# Revit family: Haworth_BeHold_OverheadStorage_Open_SingleSided
name_source: partatom
category: Furniture Systems
revit_build: Autodesk Revit 2018 (Build: 20170223_1515(x64)
units: mm (PartAtom-declared; Revit-internal decimal feet)

## family parameters
Always vertical = Yes
Cut with Voids When Loaded = No
OmniClass Number = 23.40.70.14.64.21
OmniClass Title = Systems Furniture
Part Type = Normal
Room Calculation Point = No
Round Connector Dimension = Use Diameter
Shared = No
Work Plane-Based = No

## types (4) — shared parameters
Actual Depth = 14.7 "
Assembly Code = E2020200
Back Finish = Haworth _ Laminate _ Beige H-34
Cabinet Finish = Haworth _ Laminate _ Beige H-34
Custom Size = No
Manufacturer = Haworth
Max. Height = 16 "
Max. Width = 72 "
Min. Height = 8 "
Min. Width = 24 "
Model = Haworth Be_Hold
Mounting Height = 22 "
Revision Number = 1
Size = Verify Final Dim. w/ Haworth
Standard Widths = 24, 30, 36, 42, 48, 54, 60, 66, 72in
Sustainability Info = https://www.haworth.com
URL = www.haworth.com
URL - Product = https://www.haworth.com
Warranty = http://www.haworth.com

## per-type parameters (varying)
| type | Actual Height | Actual Width | Description | Large | Small | TFL Divider | Width |
| 16h 24w | 16 " | 24 " | Haworth - Be_Hold - Overhead Storage Unit - Open - Single Sided - 16h 24w | Yes | No | No | 24 " |
| 16h 72w | 16 " | 72 " | Haworth - Be_Hold - Overhead Storage Unit - Open - Single Sided - 16h 72w | Yes | No | Yes | 72 " |
| 8h 24w | 8 " | 24 " | Haworth - Be_Hold - Overhead Storage Unit - Open - Single Sided - 8h 24w | No | Yes | No | 24 " |
| 8h 72w | 8 " | 72 " | Haworth - Be_Hold - Overhead Storage Unit - Open - Single Sided - 8h 72w | No | Yes | Yes | 72 " |

## geometry (parser evidence)
native form markers: Sweep x2
no freeform markers — native parametric forms only
